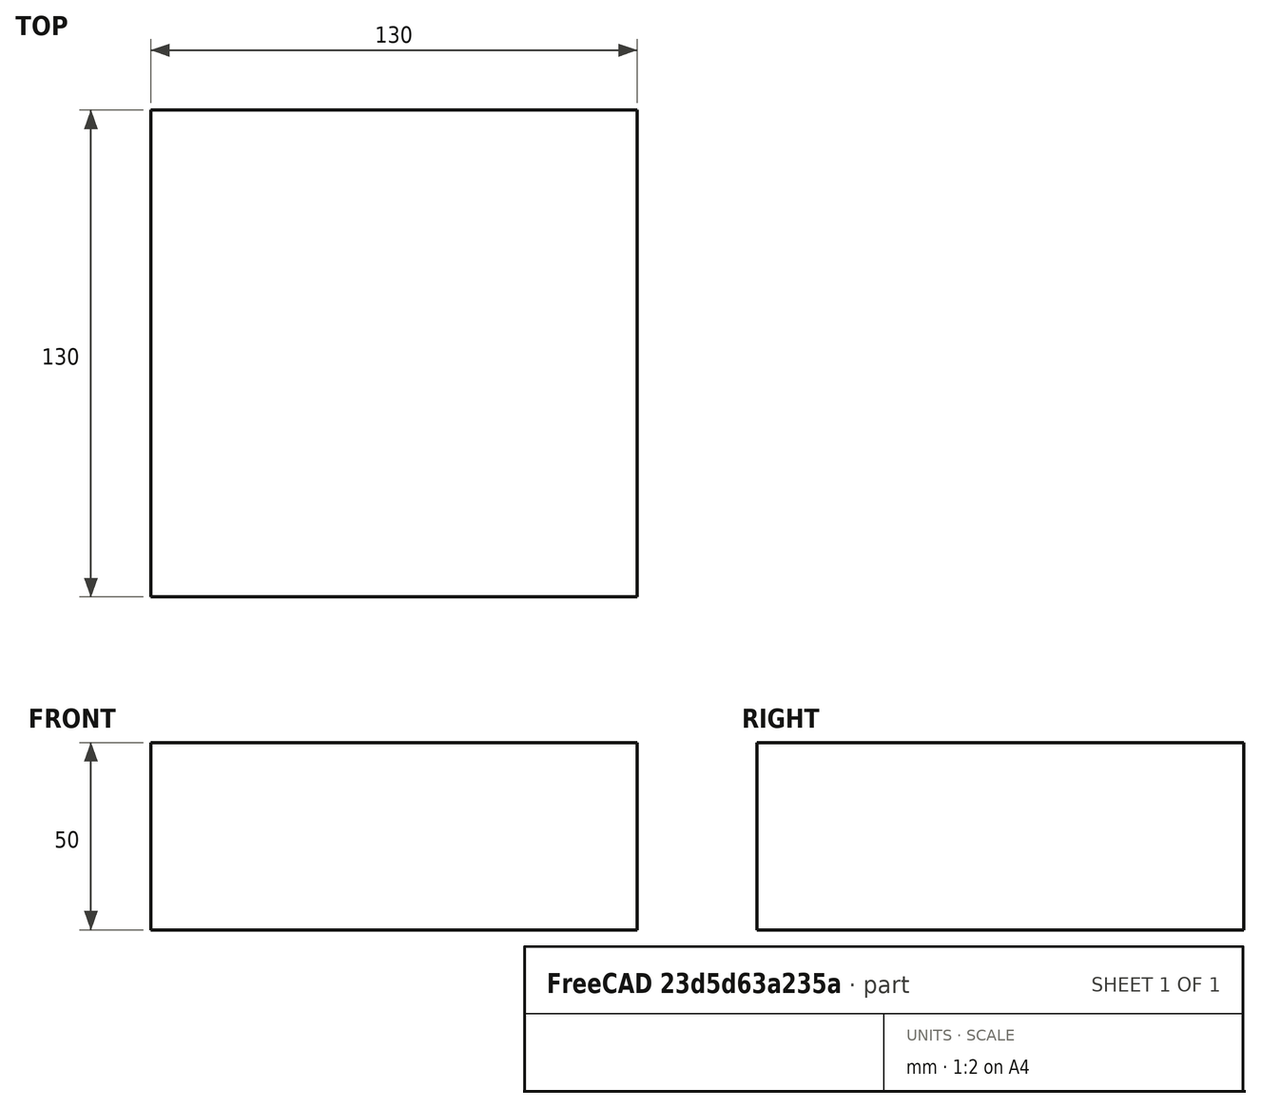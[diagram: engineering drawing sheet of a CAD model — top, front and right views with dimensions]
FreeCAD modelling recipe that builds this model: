
FCSTD DOCUMENT  (FreeCAD 0.15R4671 (Git))
Label: Square Bar 130 EN10059 S235JR
License: All rights reserved
LicenseURL: http://en.wikipedia.org/wiki/All_rights_reserved
objects: Sketcher::SketchObject×1, Part::Extrusion×1
note: 2 computed .brp shape members not serialized (recipe doc carries the construction recipe); baked Part::Feature solids carry a one-line shape summary decoded from their .brp

FEATURE [Sketcher::SketchObject] Sketch
  sketch-geometry (4):
    g0: LineSegment StartX=-65 StartY=-65 StartZ=0 EndX=65 EndY=-65 EndZ=0
    g1: LineSegment StartX=65 StartY=-65 StartZ=0 EndX=65 EndY=65 EndZ=0
    g2: LineSegment StartX=65 StartY=65 StartZ=0 EndX=-65 EndY=65 EndZ=0
    g3: LineSegment StartX=-65 StartY=65 StartZ=0 EndX=-65 EndY=-65 EndZ=0
  constraints (12):
    c: Coincident(g0,g1)
    c: Coincident(g1,g2)
    c: Coincident(g2,g3)
    c: Coincident(g3,g0)
    c: Horizontal(g0)
    c: Horizontal(g2)
    c: Vertical(g1)
    c: Vertical(g3)
    c: Symmetric(g1,g0,g-1)
    c: Symmetric(g2,g1,g-2)
    c: Equal(g1,g2)
    c: DistanceY(g1) = 130
FEATURE [Part::Extrusion] Extrude  label="Square Bar 130 EN10059 S235JR"
  Base = -> Sketch
  Dir = (0,0,50)
  Solid = true
